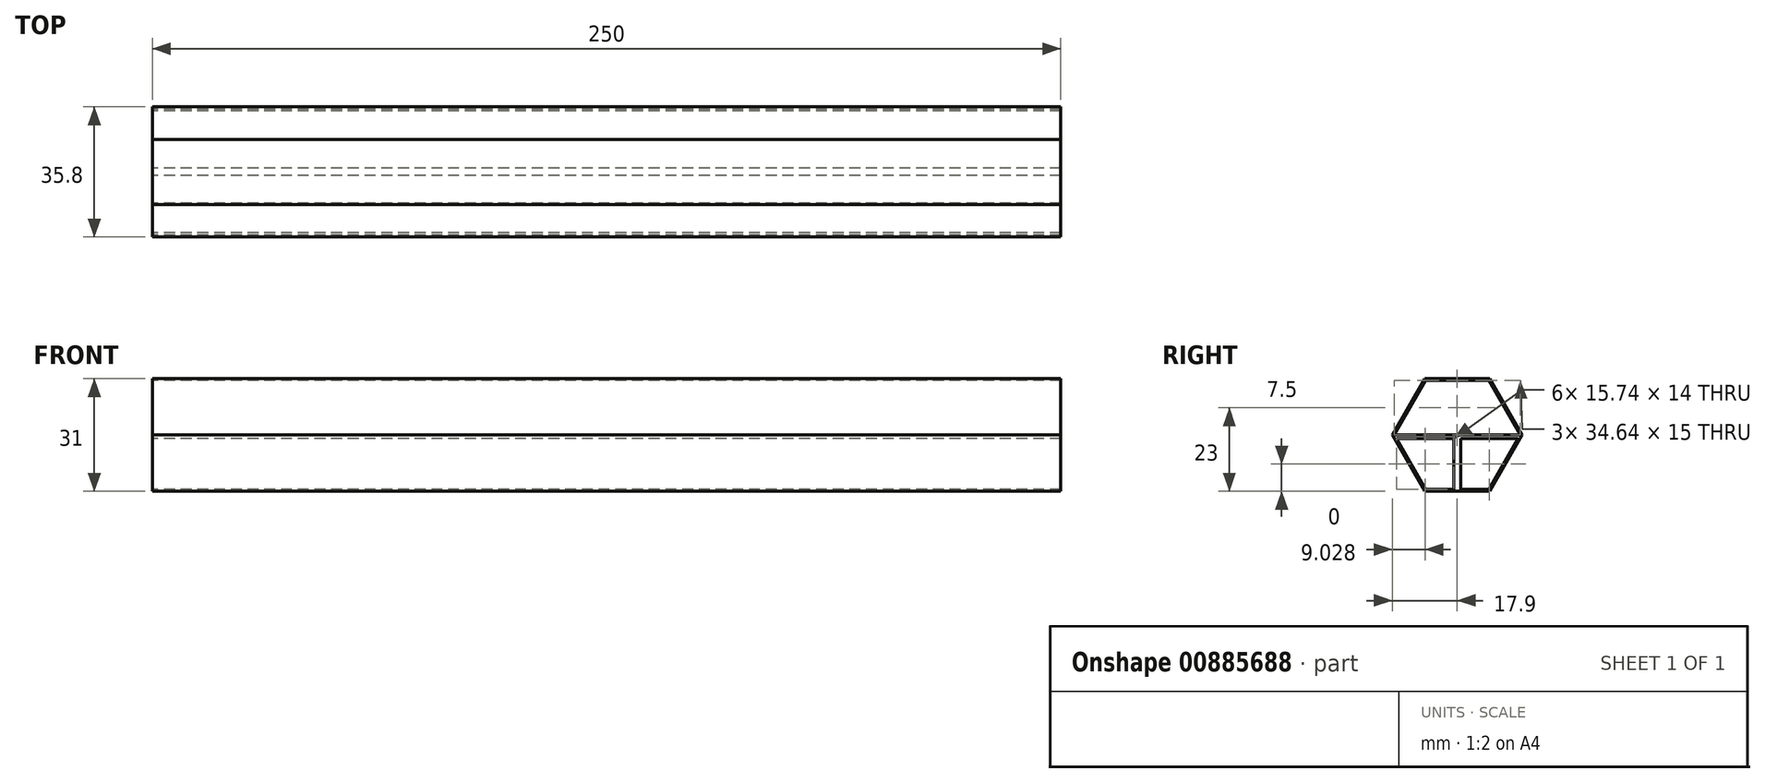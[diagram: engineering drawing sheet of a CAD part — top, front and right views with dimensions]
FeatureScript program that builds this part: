
annotation { "Feature Type Name" : "Feature", "Feature Type Description" : "" }
export const myFeature = defineFeature(function(context is Context, id is Id, definition is map)
    precondition{}
    {
        {
            var Q0;
            Q0=qCreatedBy(makeId("Right.planeOp"),FACE);
            var sketch = newSketch(context, id + "F0", { "sketchPlane" : qUnion([Q0])});
            skCircle(sketch, "E0.cCircle", {"center": v(0, 0) * mm, "radius": 15 * mm, "construction": true});
            skLineSegment(sketch, "E0.0", {"start": v(8.66, -15) * mm, "end": v(-8.66, -15) * mm});
            skLineSegment(sketch, "E0.1", {"start": v(-8.66, -15) * mm, "end": v(-17.32, 0) * mm});
            skLineSegment(sketch, "E0.2", {"start": v(-17.32, 0) * mm, "end": v(-8.66, 15) * mm});
            skLineSegment(sketch, "E0.3", {"start": v(-8.66, 15) * mm, "end": v(8.66, 15) * mm});
            skLineSegment(sketch, "E0.4", {"start": v(8.66, 15) * mm, "end": v(17.32, 0) * mm});
            skLineSegment(sketch, "E0.5", {"start": v(17.32, 0) * mm, "end": v(8.66, -15) * mm});
            skPoint(sketch, "E0.0.midPoint", {"position": v(0, -15) * mm});
            skCircle(sketch, "E1.cCircle", {"center": v(0, 0) * mm, "radius": 15.5 * mm, "construction": true});
            skLineSegment(sketch, "E1.0", {"start": v(17.9, 0) * mm, "end": v(8.95, -15.5) * mm});
            skLineSegment(sketch, "E1.1", {"start": v(8.95, -15.5) * mm, "end": v(-8.95, -15.5) * mm});
            skLineSegment(sketch, "E1.2", {"start": v(-8.95, -15.5) * mm, "end": v(-17.9, 0) * mm});
            skLineSegment(sketch, "E1.3", {"start": v(-17.9, 0) * mm, "end": v(-8.95, 15.5) * mm});
            skLineSegment(sketch, "E1.4", {"start": v(-8.95, 15.5) * mm, "end": v(8.95, 15.5) * mm});
            skLineSegment(sketch, "E1.5", {"start": v(8.95, 15.5) * mm, "end": v(17.9, 0) * mm});
            skPoint(sketch, "E1.0.midPoint", {"position": v(13.42, -7.75) * mm});
            skLineSegment(sketch, "E2", {"start": v(-17.32, 0) * mm, "end": v(17.32, 0) * mm});
            skLineSegment(sketch, "E3.0", {"start": v(-17.32, -1) * mm, "end": v(17.32, -1) * mm});
            skLineSegment(sketch, "E4", {"start": v(0, 0) * mm, "end": v(0, -15) * mm, "construction": true});
            skLineSegment(sketch, "E5.0", {"start": v(1, 0) * mm, "end": v(1, -15) * mm});
            skLineSegment(sketch, "E6.0", {"start": v(-1, 0) * mm, "end": v(-1, -15) * mm});
            skSolve(sketch);
        }
        {
            var Q0;
            Q0 = qSketchRegion(id + "F0", true);
            var Q1;
            {var subQ1=sQuery(id+"F0.wireOp",EDGE,"E0.1");var subQ3=sQuery(id+"F0.wireOp",EDGE,"E3.0");var subQ4=makeQuery(id+"F0.imprint","INTERSECT",VERTEX,{"derivedFrom":[subQ1,subQ3]});Q1=makeQuery(id+"F0.imprint","IMPRINT",FACE,{"disambiguationData":[TD([[makeQuery(id+"F0.imprint","IMPRINT",EDGE,{"disambiguationData":[TD([[subQ4,-1.0]])],"derivedFrom":subQ3}),1.0]])]});}
            var Q2;
            {var subQ0=sQuery(id+"F0.wireOp",EDGE,"E5.0");var subQ1=sQuery(id+"F0.wireOp",EDGE,"E0.0");var subQ2=makeQuery(id+"F0.imprint","INTERSECT",VERTEX,{"derivedFrom":[subQ1,subQ0]});Q2=makeQuery(id+"F0.imprint","IMPRINT",FACE,{"disambiguationData":[TD([[makeQuery(id+"F0.imprint","IMPRINT",EDGE,{"disambiguationData":[TD([[subQ2,-1.0]])],"derivedFrom":subQ1}),-1.0]])]});}
            var Q3;
            {var subQ0=sQuery(id+"F0.wireOp",EDGE,"E5.0");var subQ1=sQuery(id+"F0.wireOp",EDGE,"E2");var subQ2=makeQuery(id+"F0.imprint","INTERSECT",VERTEX,{"derivedFrom":[subQ1,subQ0]});Q3=makeQuery(id+"F0.imprint","IMPRINT",FACE,{"disambiguationData":[TD([[makeQuery(id+"F0.imprint","IMPRINT",EDGE,{"disambiguationData":[TD([[subQ2,1.0]])],"derivedFrom":subQ1}),-1.0]])]});}
            var Q4;
            {var subQ1=sQuery(id+"F0.wireOp",EDGE,"E0.5");var subQ3=sQuery(id+"F0.wireOp",EDGE,"E3.0");var subQ4=makeQuery(id+"F0.imprint","INTERSECT",VERTEX,{"derivedFrom":[subQ1,subQ3]});Q4=makeQuery(id+"F0.imprint","IMPRINT",FACE,{"disambiguationData":[TD([[makeQuery(id+"F0.imprint","IMPRINT",EDGE,{"disambiguationData":[TD([[subQ4,1.0]])],"derivedFrom":subQ3}),1.0]])]});}
            extrude(context, id + "F1", {"entities" : qUnion([Q0, Q1, Q2, Q3, Q4]), "depth" : 250 * mm, "offsetDistance" : 25 * mm});
        }
    });
